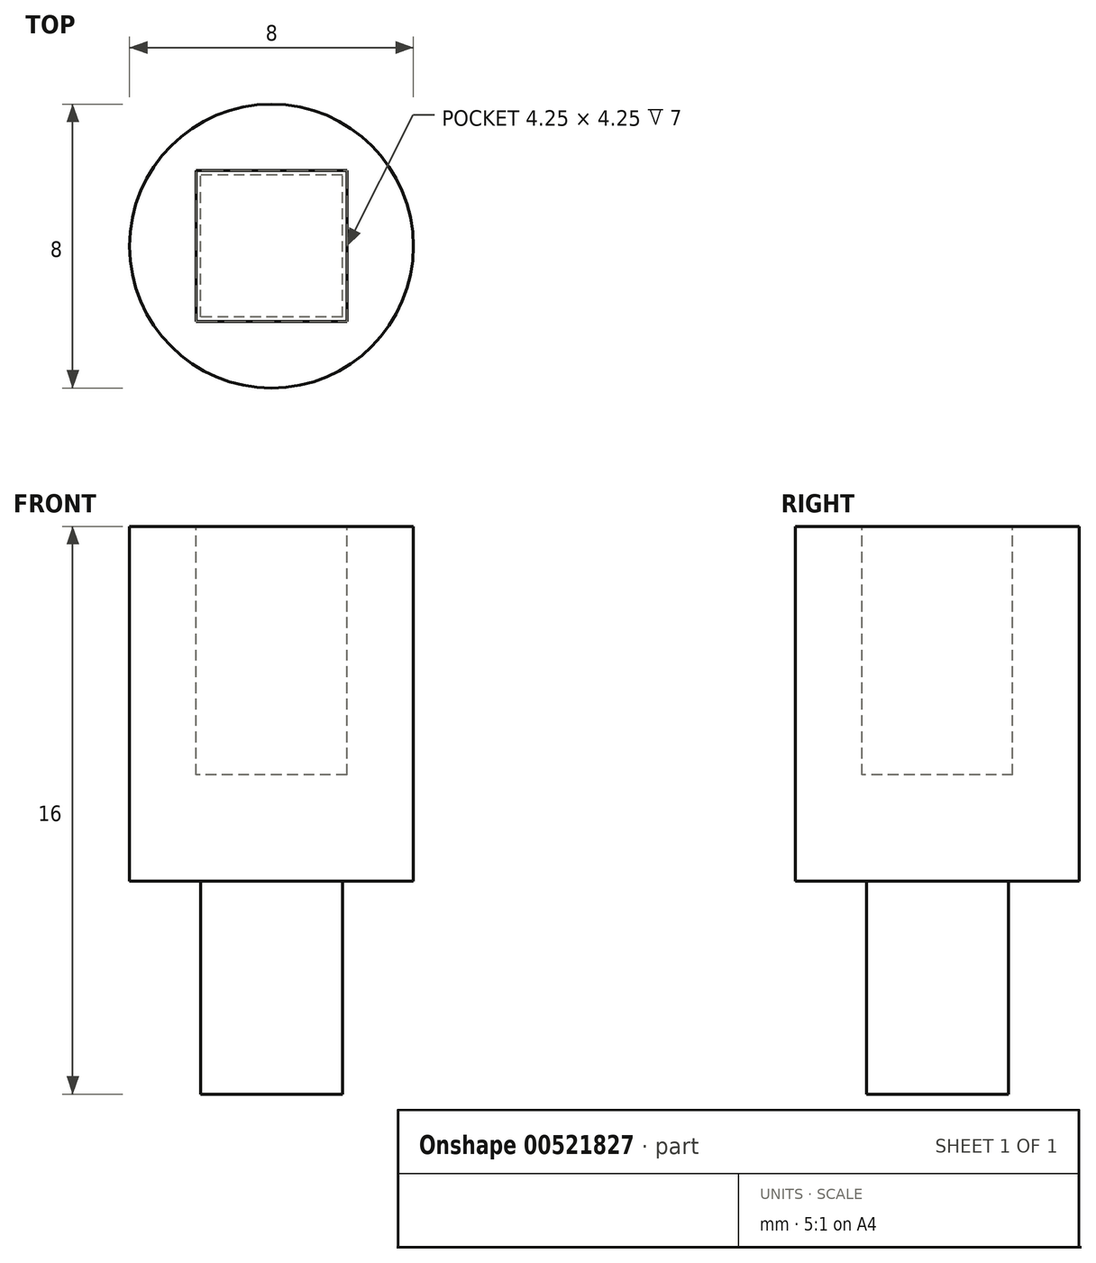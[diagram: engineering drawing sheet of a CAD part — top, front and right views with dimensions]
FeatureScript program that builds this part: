
annotation { "Feature Type Name" : "Feature", "Feature Type Description" : "" }
export const myFeature = defineFeature(function(context is Context, id is Id, definition is map)
    precondition{}
    {
        {
            var Q0;
            Q0=qCreatedBy(makeId("Top.planeOp"),FACE);
            var sketch = newSketch(context, id + "F0", { "sketchPlane" : qUnion([Q0])});
            skCircle(sketch, "E0", {"center": v(0, 0) * mm, "radius": 4 * mm});
            skLineSegment(sketch, "E1.bottom", {"start": v(2, -2) * mm, "end": v(-2, -2) * mm});
            skLineSegment(sketch, "E1.top", {"start": v(2, 2) * mm, "end": v(-2, 2) * mm});
            skLineSegment(sketch, "E1.left", {"start": v(2, -2) * mm, "end": v(2, 2) * mm});
            skLineSegment(sketch, "E1.right", {"start": v(-2, -2) * mm, "end": v(-2, 2) * mm});
            skSolve(sketch);
        }
        {
            var Q0;
            Q0=makeQuery(id+"F0.imprint","IMPRINT",FACE,{"disambiguationData":[TD([[makeQuery(id+"F0.imprint","IMPRINT",EDGE,{"derivedFrom":sQuery(id+"F0.wireOp",EDGE,"E0")}),1.0]])]});
            var Q1;
            Q1=makeQuery(id+"F0.imprint","IMPRINT",FACE,{"disambiguationData":[TD([[makeQuery(id+"F0.imprint","IMPRINT",EDGE,{"derivedFrom":sQuery(id+"F0.wireOp",EDGE,"E1.bottom")}),-1.0]])]});
            extrude(context, id + "F1", {"entities" : qUnion([Q0, Q1]), "depth" : 10 * mm, "offsetDistance" : 25 * mm});
        }
        {
            var Q0;
            Q0=makeQuery(id+"F1.opExtrude","CAP_FACE",FACE,{"disambiguationData":[OSD([sQuery(id+"F0.wireOp",EDGE,"E0")])],"isStart":false});
            var sketch = newSketch(context, id + "F2", { "sketchPlane" : qUnion([Q0])});
            skLineSegment(sketch, "E2.bottom", {"start": v(2.12, 2.12) * mm, "end": v(-2.13, 2.12) * mm});
            skLineSegment(sketch, "E2.top", {"start": v(2.13, -2.13) * mm, "end": v(-2.12, -2.13) * mm});
            skLineSegment(sketch, "E2.left", {"start": v(2.12, 2.12) * mm, "end": v(2.13, -2.13) * mm});
            skLineSegment(sketch, "E2.right", {"start": v(-2.13, 2.12) * mm, "end": v(-2.12, -2.13) * mm});
            skPoint(sketch, "E2.middle", {"position": v(0, 0) * mm});
            skSolve(sketch);
        }
        {
            var Q0;
            Q0=makeQuery(id+"F2.imprint","IMPRINT",FACE,{"disambiguationData":[TD([[makeQuery(id+"F2.imprint","IMPRINT",EDGE,{"derivedFrom":sQuery(id+"F2.wireOp",EDGE,"E2.bottom")}),1.0]])]});
            extrude(context, id + "F3", {"entities" : qUnion([Q0]), "operationType" : NewBodyOperationType.REMOVE, "oppositeDirection" : true, "depth" : 7 * mm, "offsetDistance" : 25 * mm});
        }
        {
            var Q0;
            Q0=makeQuery(id+"F0.imprint","IMPRINT",FACE,{"disambiguationData":[TD([[makeQuery(id+"F0.imprint","IMPRINT",EDGE,{"derivedFrom":sQuery(id+"F0.wireOp",EDGE,"E1.bottom")}),-1.0]])]});
            extrude(context, id + "F4", {"entities" : qUnion([Q0]), "operationType" : NewBodyOperationType.ADD, "oppositeDirection" : true, "depth" : 6 * mm, "offsetDistance" : 25 * mm});
        }
    });
